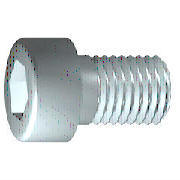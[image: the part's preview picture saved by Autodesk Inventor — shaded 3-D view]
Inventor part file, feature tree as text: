
AUTODESK INVENTOR PART (.ipt)
format: ipt  version: 2023.3 (Build 273359000, 359)  size: 197,120 bytes
history: native  units: mm (DEFAULTED — no unit token found)
features: sketch x2, other x1, extrude x1, plane x1, fillet x1
ambient origin geometry x7: Origin, YZ Plane, XY Plane, X Axis, Y Axis, Z Axis, Center Point
bodies: Solid1 (feature_tree)
feature tree (6):
  other  "Körper"
  extrude  "Loch"  Depth=100.0mm
  plane  "Work Plane1"
  fillet  "Fillet2"  Radius=100.0mm
  sketch  "Skizze1"  dims[d1=135.0mm d2=3.6808mm d3=100.0mm]
  sketch  "Skizze2"  dims[d4=60.0mm d5=60.0deg d6=100.0mm d7=100.0mm d8=98.149546mm d9=150.0mm d10=90.0deg d11=10.0mm d12=0.0mm d13=135.0mm d14=0.0mm d15=3.6807mm d16=3.6807mm d17=10.0mm d19=0.0mm d26=150.0mm d27=45.0deg d28=0.0mm d29=0.0mm d30=2.5mm]
